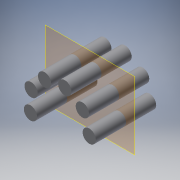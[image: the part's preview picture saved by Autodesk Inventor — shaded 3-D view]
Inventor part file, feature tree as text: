
AUTODESK INVENTOR PART (.ipt)
format: ipt  version: 2019 (Build 230136000, 136)  size: 112,640 bytes
history: native  units: mm
features: other x3, plane x1, extrude x1, sketch x1, reference x1
ambient origin geometry x8: Origin, YZ Plane, XZ Plane, XY Plane, X Axis, Y Axis, Z Axis, Center Point
bodies: Solid1 (feature_tree)
feature tree (7):
  plane  "Work Plane1"
  extrude  "Extrusion1"  [1 undecoded]
  sketch  "Sketch1"  dims[d0=50.0mm d1=0.0mm]
  reference  "Reference1"
  parser-record x1  (decoder bookkeeping rows leaked as tree rows — omitted from the tree; the rows remain in map.json)
  other  "mount assem.iam"
  other  "mounter:1"
note: 1 required parameter value undecoded (feature->parameter linkage not recoverable at this tier; creation-order binding heuristic only, values carry confidence <= 0.55)
note: 1 file-system path scrubbed to <path> (originals preserved in map.json)
